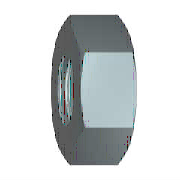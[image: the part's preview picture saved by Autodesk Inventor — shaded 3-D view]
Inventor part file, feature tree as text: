
AUTODESK INVENTOR PART (.ipt)
format: ipt  version: 2023 (Build 270158000, 158)  size: 163,328 bytes
history: native  units: mm (DEFAULTED — no unit token found)
features: sketch x3, other x2, extrude x1, hole x1, plane x1
ambient origin geometry x7: Origin, YZ Plane, XZ Plane, X Axis, Y Axis, Z Axis, Center Point
bodies: Solid1 (feature_tree)
feature tree (8):
  extrude  "Базовый элемент"  Depth=18.475209mm
  other  "Фаска1"
  hole  "Резьба"  [1 undecoded]
  other  "Work Axis1"
  plane  "Work Plane1"
  sketch  "Эскиз1"
  sketch  "Эскиз2"
  sketch  "Эскиз3"
note: 1 required parameter value undecoded (feature->parameter linkage not recoverable at this tier; creation-order binding heuristic only, values carry confidence <= 0.55)
